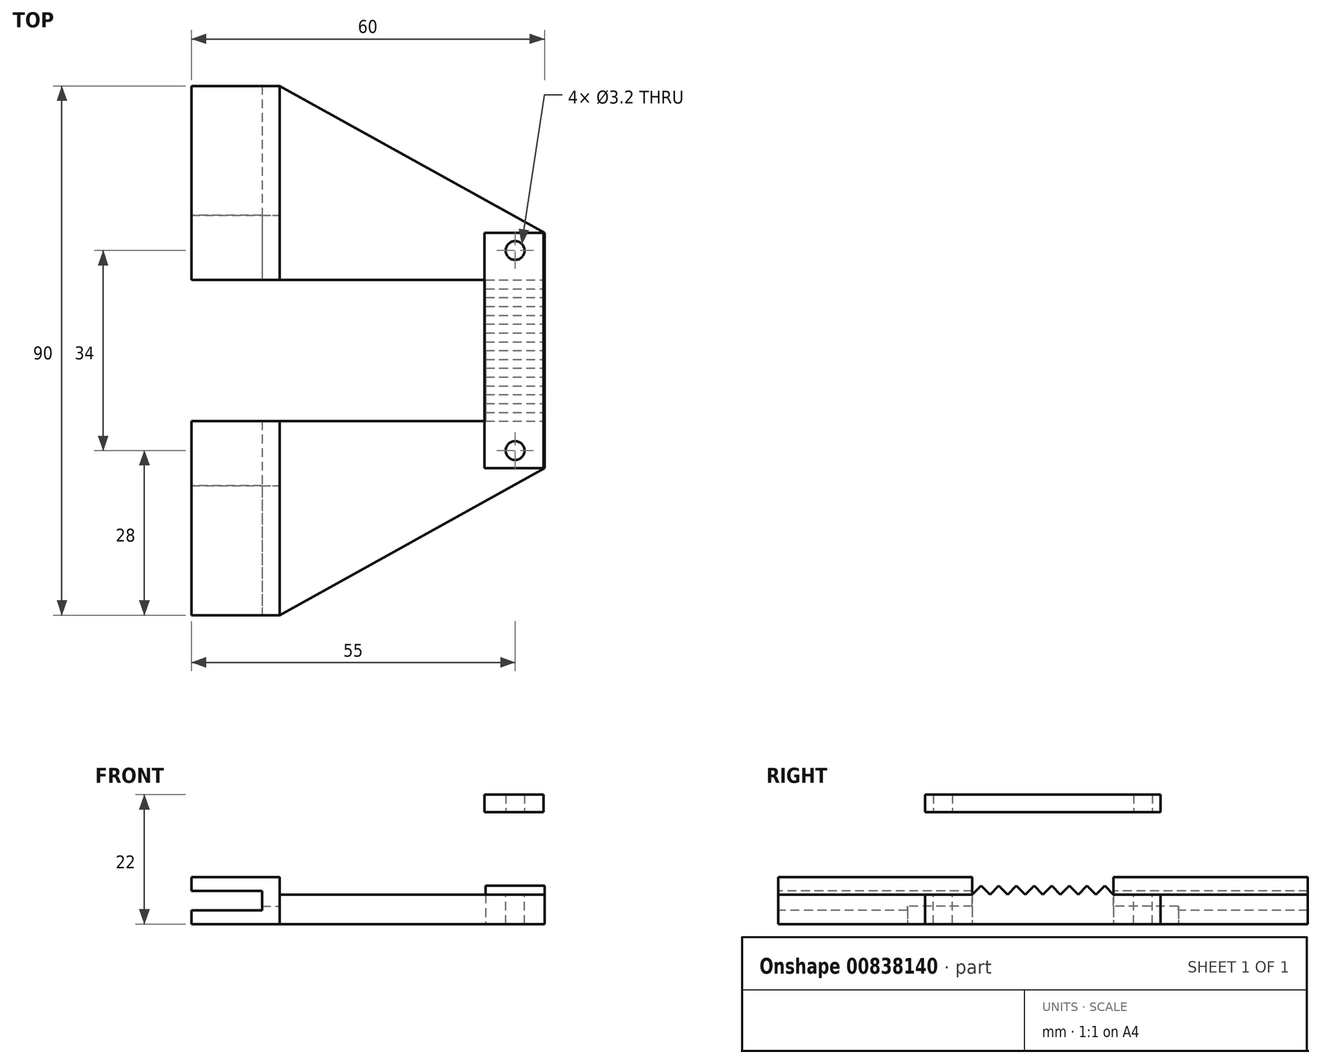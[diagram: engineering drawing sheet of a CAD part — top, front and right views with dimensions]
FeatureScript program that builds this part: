
annotation { "Feature Type Name" : "Feature", "Feature Type Description" : "" }
export const myFeature = defineFeature(function(context is Context, id is Id, definition is map)
    precondition{}
    {
        {
            var Q0;
            Q0=qCreatedBy(makeId("Right.planeOp"),FACE);
            var sketch = newSketch(context, id + "F0", { "sketchPlane" : qUnion([Q0])});
            skLineSegment(sketch, "E0.bottom", {"start": v(-45, 4) * mm, "end": v(45, 4) * mm});
            skLineSegment(sketch, "E0.top", {"start": v(-45, -4) * mm, "end": v(45, -4) * mm});
            skLineSegment(sketch, "E0.left", {"start": v(-45, 4) * mm, "end": v(-45, -4) * mm});
            skLineSegment(sketch, "E0.right", {"start": v(45, 4) * mm, "end": v(45, -4) * mm});
            skLineSegment(sketch, "E1", {"start": v(-45, 4) * mm, "end": v(45, -4) * mm, "construction": true});
            skLineSegment(sketch, "E2", {"start": v(45, 4) * mm, "end": v(-45, -4) * mm, "construction": true});
            skPoint(sketch, "E3", {"position": v(0, 0) * mm});
            skSolve(sketch);
        }
        {
            var Q0;
            Q0 = qSketchRegion(id + "F0", true);
            extrude(context, id + "F1", {"entities" : qUnion([Q0]), "oppositeDirection" : true, "depth" : 15 * mm, "offsetDistance" : 25 * mm});
        }
        {
            var Q0;
            Q0=makeQuery(id+"F1.opExtrude","CAP_FACE",FACE,{"disambiguationData":[OSD([sQuery(id+"F0.wireOp",EDGE,"E0.bottom"),sQuery(id+"F0.wireOp",EDGE,"E0.top"),sQuery(id+"F0.wireOp",EDGE,"E0.left"),sQuery(id+"F0.wireOp",EDGE,"E0.right")])],"isStart":false});
            var sketch = newSketch(context, id + "F2", { "sketchPlane" : qUnion([Q0])});
            skLineSegment(sketch, "E4.bottom", {"start": v(-45, 1.65) * mm, "end": v(45, 1.65) * mm});
            skLineSegment(sketch, "E4.top", {"start": v(-45, -1.65) * mm, "end": v(45, -1.65) * mm});
            skLineSegment(sketch, "E4.left", {"start": v(-45, 1.65) * mm, "end": v(-45, -1.65) * mm});
            skLineSegment(sketch, "E4.right", {"start": v(45, 1.65) * mm, "end": v(45, -1.65) * mm});
            skLineSegment(sketch, "E5", {"start": v(-45, 1.65) * mm, "end": v(45, -1.65) * mm, "construction": true});
            skLineSegment(sketch, "E6", {"start": v(45, 1.65) * mm, "end": v(-45, -1.65) * mm, "construction": true});
            skPoint(sketch, "E7", {"position": v(0, 0) * mm});
            skSolve(sketch);
        }
        {
            var Q0;
            Q0 = qSketchRegion(id + "F2", true);
            extrude(context, id + "F3", {"entities" : qUnion([Q0]), "operationType" : NewBodyOperationType.REMOVE, "oppositeDirection" : true, "depth" : 12 * mm, "offsetDistance" : 25 * mm});
        }
        {
            var Q0;
            Q0=makeQuery(id+"F1.opExtrude","CAP_FACE",FACE,{"disambiguationData":[OSD([sQuery(id+"F0.wireOp",EDGE,"E0.bottom"),sQuery(id+"F0.wireOp",EDGE,"E0.top"),sQuery(id+"F0.wireOp",EDGE,"E0.left"),sQuery(id+"F0.wireOp",EDGE,"E0.right")])],"isStart":true});
            var sketch = newSketch(context, id + "F4", { "sketchPlane" : qUnion([Q0])});
            skLineSegment(sketch, "E8.bottom", {"start": v(-12, 4) * mm, "end": v(12, 4) * mm});
            skLineSegment(sketch, "E8.top", {"start": v(-12, -1) * mm, "end": v(12, -1) * mm});
            skLineSegment(sketch, "E8.left", {"start": v(-12, 4) * mm, "end": v(-12, -1) * mm});
            skLineSegment(sketch, "E8.right", {"start": v(12, 4) * mm, "end": v(12, -1) * mm});
            skSolve(sketch);
        }
        {
            var Q0;
            Q0 = qSketchRegion(id + "F4", true);
            extrude(context, id + "F5", {"entities" : qUnion([Q0]), "operationType" : NewBodyOperationType.REMOVE, "oppositeDirection" : true, "depth" : 15 * mm, "offsetDistance" : 25 * mm});
        }
        {
            var Q0;
            Q0=makeQuery(id+"F1.opExtrude","CAP_FACE",FACE,{"disambiguationData":[OSD([sQuery(id+"F0.wireOp",EDGE,"E0.bottom"),sQuery(id+"F0.wireOp",EDGE,"E0.top"),sQuery(id+"F0.wireOp",EDGE,"E0.left"),sQuery(id+"F0.wireOp",EDGE,"E0.right")])],"isStart":true});
            var sketch = newSketch(context, id + "F6", { "sketchPlane" : qUnion([Q0])});
            skLineSegment(sketch, "E9.bottom", {"start": v(-23, -1) * mm, "end": v(23, -1) * mm});
            skLineSegment(sketch, "E9.top", {"start": v(-23, -4) * mm, "end": v(23, -4) * mm});
            skLineSegment(sketch, "E9.left", {"start": v(-23, -1) * mm, "end": v(-23, -4) * mm});
            skLineSegment(sketch, "E9.right", {"start": v(23, -1) * mm, "end": v(23, -4) * mm});
            skSolve(sketch);
        }
        {
            var Q0;
            Q0 = qSketchRegion(id + "F6", true);
            extrude(context, id + "F7", {"entities" : qUnion([Q0]), "operationType" : NewBodyOperationType.REMOVE, "oppositeDirection" : true, "depth" : 18 * mm, "offsetDistance" : 25 * mm});
        }
        {
            var Q0;
            Q0=makeQuery(id+"F1.opExtrude","CAP_FACE",FACE,{"disambiguationData":[OSD([sQuery(id+"F0.wireOp",EDGE,"E0.bottom"),sQuery(id+"F0.wireOp",EDGE,"E0.top"),sQuery(id+"F0.wireOp",EDGE,"E0.left"),sQuery(id+"F0.wireOp",EDGE,"E0.right")])],"isStart":true});
            var sketch = newSketch(context, id + "F8", { "sketchPlane" : qUnion([Q0])});
            skLineSegment(sketch, "E10.bottom", {"start": v(12, 2) * mm, "end": v(-12, 2) * mm});
            skLineSegment(sketch, "E10.top", {"start": v(-12, -4) * mm, "end": v(12, -4) * mm});
            skLineSegment(sketch, "E10.left", {"start": v(-12, 2) * mm, "end": v(-12, -4) * mm});
            skLineSegment(sketch, "E10.right", {"start": v(12, 2) * mm, "end": v(12, -4) * mm});
            skSolve(sketch);
        }
        {
            var Q0;
            Q0 = qSketchRegion(id + "F8", true);
            extrude(context, id + "F9", {"entities" : qUnion([Q0]), "operationType" : NewBodyOperationType.REMOVE, "oppositeDirection" : true, "depth" : 15 * mm, "offsetDistance" : 25 * mm});
        }
        {
            var Q0;
            {var subQ1=sQuery(id+"F0.wireOp",EDGE,"E0.left");var subQ2=sQuery(id+"F0.wireOp",EDGE,"E0.top");Q0=makeQuery(id+"F9.boolean.opBoolean","SPLIT",FACE,{"disambiguationData":[TD([makeQuery(id+"F1.opExtrude","SWEPT_FACE",FACE,{"disambiguationData":[OSD([subQ1])]})])],"derivedFrom":makeQuery(id+"F1.opExtrude","SWEPT_FACE",FACE,{"disambiguationData":[OSD([subQ2])]})});}
            var sketch = newSketch(context, id + "F10", { "sketchPlane" : qUnion([Q0])});
            skLineSegment(sketch, "E11", {"start": v(0, 45) * mm, "end": v(45, 20) * mm});
            skLineSegment(sketch, "E12", {"start": v(45, 20) * mm, "end": v(45, 0) * mm});
            skLineSegment(sketch, "E13", {"start": v(45, 0) * mm, "end": v(35, 0) * mm});
            skLineSegment(sketch, "E14", {"start": v(35, 0) * mm, "end": v(35, 12) * mm});
            skLineSegment(sketch, "E15", {"start": v(-1.98, 12) * mm, "end": v(61.46, 12) * mm, "construction": true});
            skLineSegment(sketch, "E16", {"start": v(0, 45) * mm, "end": v(0, 12) * mm});
            skLineSegment(sketch, "E17", {"start": v(0, 12) * mm, "end": v(35, 12) * mm});
            skLineSegment(sketch, "E18.MirrorCS", {"start": v(0, -12) * mm, "end": v(35, -12) * mm});
            skLineSegment(sketch, "E19.MirrorCS", {"start": v(45, -20) * mm, "end": v(45, 0) * mm});
            skLineSegment(sketch, "E20.MirrorCS", {"start": v(-1.98, -12) * mm, "end": v(61.46, -12) * mm, "construction": true});
            skLineSegment(sketch, "E21.MirrorCS", {"start": v(0, -45) * mm, "end": v(0, -12) * mm});
            skLineSegment(sketch, "E22.MirrorCS", {"start": v(0, -45) * mm, "end": v(45, -20) * mm});
            skLineSegment(sketch, "E23.MirrorCS", {"start": v(35, 0) * mm, "end": v(35, -12) * mm});
            skSolve(sketch);
        }
        {
            var Q0;
            Q0 = qSketchRegion(id + "F10", true);
            extrude(context, id + "F11", {"entities" : qUnion([Q0]), "operationType" : NewBodyOperationType.ADD, "oppositeDirection" : true, "depth" : 5 * mm, "offsetDistance" : 25 * mm});
        }
        {
            var Q0;
            Q0=makeQuery(id+"F11.opExtrude","CAP_FACE",FACE,{"disambiguationData":[OSD([sQuery(id+"F10.wireOp",EDGE,"E11"),sQuery(id+"F10.wireOp",EDGE,"E12"),sQuery(id+"F10.wireOp",EDGE,"E14"),sQuery(id+"F10.wireOp",EDGE,"E16"),sQuery(id+"F10.wireOp",EDGE,"E17"),sQuery(id+"F10.wireOp",EDGE,"E18.MirrorCS"),sQuery(id+"F10.wireOp",EDGE,"E19.MirrorCS"),sQuery(id+"F10.wireOp",EDGE,"E21.MirrorCS"),sQuery(id+"F10.wireOp",EDGE,"E22.MirrorCS"),sQuery(id+"F10.wireOp",EDGE,"E23.MirrorCS")])],"isStart":false});
            var sketch = newSketch(context, id + "F12", { "sketchPlane" : qUnion([Q0])});
            skLineSegment(sketch, "E24", {"start": v(40, 27.1) * mm, "end": v(40, -30.08) * mm, "construction": true});
            skCircle(sketch, "E25", {"center": v(40, 17) * mm, "radius": 1.6 * mm});
            skCircle(sketch, "E26.MirrorC", {"center": v(40, -17) * mm, "radius": 1.6 * mm});
            skSolve(sketch);
        }
        {
            var Q0;
            Q0 = qSketchRegion(id + "F12", true);
            extrude(context, id + "F13", {"entities" : qUnion([Q0]), "operationType" : NewBodyOperationType.REMOVE, "oppositeDirection" : true, "depth" : 5 * mm, "offsetDistance" : 25 * mm});
        }
        {
            var Q0;
            Q0=makeQuery(id+"F11.opExtrude","SWEPT_FACE",FACE,{"disambiguationData":[OSD([sQuery(id+"F10.wireOp",EDGE,"E12"),sQuery(id+"F10.wireOp",EDGE,"E19.MirrorCS")])]});
            var sketch = newSketch(context, id + "F14", { "sketchPlane" : qUnion([Q0])});
            skLineSegment(sketch, "E27", {"start": v(101, -18.43) * mm, "end": v(105.3, -18.43) * mm});
            skLineSegment(sketch, "E28", {"start": v(0, 1) * mm, "end": v(1.5, 2.5) * mm});
            skLineSegment(sketch, "E29", {"start": v(1.5, 2.5) * mm, "end": v(3, 1) * mm});
            skLineSegment(sketch, "E30", {"start": v(3, 1) * mm, "end": v(0, 1) * mm});
            skLineSegment(sketch, "E31.1.0.0", {"start": v(6, 1) * mm, "end": v(3, 1) * mm});
            skLineSegment(sketch, "E31.1.0.1", {"start": v(4.5, 2.5) * mm, "end": v(6, 1) * mm});
            skLineSegment(sketch, "E31.1.0.2", {"start": v(3, 1) * mm, "end": v(4.5, 2.5) * mm});
            skLineSegment(sketch, "E31.2.0.0", {"start": v(9, 1) * mm, "end": v(6, 1) * mm});
            skLineSegment(sketch, "E31.2.0.1", {"start": v(7.5, 2.5) * mm, "end": v(9, 1) * mm});
            skLineSegment(sketch, "E31.2.0.2", {"start": v(6, 1) * mm, "end": v(7.5, 2.5) * mm});
            skLineSegment(sketch, "E31.3.0.0", {"start": v(12, 1) * mm, "end": v(9, 1) * mm});
            skLineSegment(sketch, "E31.3.0.1", {"start": v(10.5, 2.5) * mm, "end": v(12, 1) * mm});
            skLineSegment(sketch, "E31.3.0.2", {"start": v(9, 1) * mm, "end": v(10.5, 2.5) * mm});
            skLineSegment(sketch, "E31.direction1", {"start": v(0, 1) * mm, "end": v(3, 1) * mm, "construction": true});
            skLineSegment(sketch, "E32.MirrorCS", {"start": v(-4.5, 2.5) * mm, "end": v(-6, 1) * mm});
            skLineSegment(sketch, "E33.MirrorCS", {"start": v(-3, 1) * mm, "end": v(0, 1) * mm});
            skLineSegment(sketch, "E34.MirrorCS", {"start": v(-7.5, 2.5) * mm, "end": v(-9, 1) * mm});
            skLineSegment(sketch, "E35.MirrorCS", {"start": v(-12, 1) * mm, "end": v(-9, 1) * mm});
            skLineSegment(sketch, "E36.MirrorCS", {"start": v(-6, 1) * mm, "end": v(-7.5, 2.5) * mm});
            skLineSegment(sketch, "E37.MirrorCS", {"start": v(-10.5, 2.5) * mm, "end": v(-12, 1) * mm});
            skLineSegment(sketch, "E38.MirrorCS", {"start": v(-6, 1) * mm, "end": v(-3, 1) * mm});
            skLineSegment(sketch, "E39.MirrorCS", {"start": v(-3, 1) * mm, "end": v(-4.5, 2.5) * mm});
            skLineSegment(sketch, "E40.MirrorCS", {"start": v(0, 1) * mm, "end": v(-3, 1) * mm, "construction": true});
            skLineSegment(sketch, "E41.MirrorCS", {"start": v(-9, 1) * mm, "end": v(-6, 1) * mm});
            skLineSegment(sketch, "E42.MirrorCS", {"start": v(0, 1) * mm, "end": v(-1.5, 2.5) * mm});
            skLineSegment(sketch, "E43.MirrorCS", {"start": v(-1.5, 2.5) * mm, "end": v(-3, 1) * mm});
            skLineSegment(sketch, "E44.MirrorCS", {"start": v(-9, 1) * mm, "end": v(-10.5, 2.5) * mm});
            skSolve(sketch);
        }
        {
            var Q0;
            Q0 = qSketchRegion(id + "F14", true);
            extrude(context, id + "F15", {"entities" : qUnion([Q0]), "operationType" : NewBodyOperationType.ADD, "oppositeDirection" : true, "depth" : 10 * mm, "offsetDistance" : 25 * mm});
        }
        {
            var Q0;
            Q0=qCreatedBy(makeId("Top.planeOp"),FACE);
            cPlane(context, id + "F16", {"entities" : qUnion([Q0]), "cplaneType" : CPlaneType.OFFSET, "offset" : 15 * mm, "width" : 150 * mm, "height" : 150 * mm});
        }
        {
            var Q0;
            Q0=qCreatedBy(id+"F16.planeOp",FACE);
            var sketch = newSketch(context, id + "F17", { "sketchPlane" : qUnion([Q0])});
            skLineSegment(sketch, "E45.bottom", {"start": v(34.8, 20) * mm, "end": v(44.8, 20) * mm});
            skLineSegment(sketch, "E45.top", {"start": v(34.8, -20) * mm, "end": v(44.8, -20) * mm});
            skLineSegment(sketch, "E45.left", {"start": v(34.8, 20) * mm, "end": v(34.8, -20) * mm});
            skLineSegment(sketch, "E45.right", {"start": v(44.8, 20) * mm, "end": v(44.8, -20) * mm});
            skCircle(sketch, "E46", {"center": v(40, 17) * mm, "radius": 1.6 * mm});
            skCircle(sketch, "E47.MirrorC", {"center": v(40, -17) * mm, "radius": 1.6 * mm});
            skSolve(sketch);
        }
        {
            var Q0;
            Q0 = qSketchRegion(id + "F17", true);
            extrude(context, id + "F18", {"entities" : qUnion([Q0]), "depth" : 3 * mm, "offsetDistance" : 25 * mm});
        }
    });
